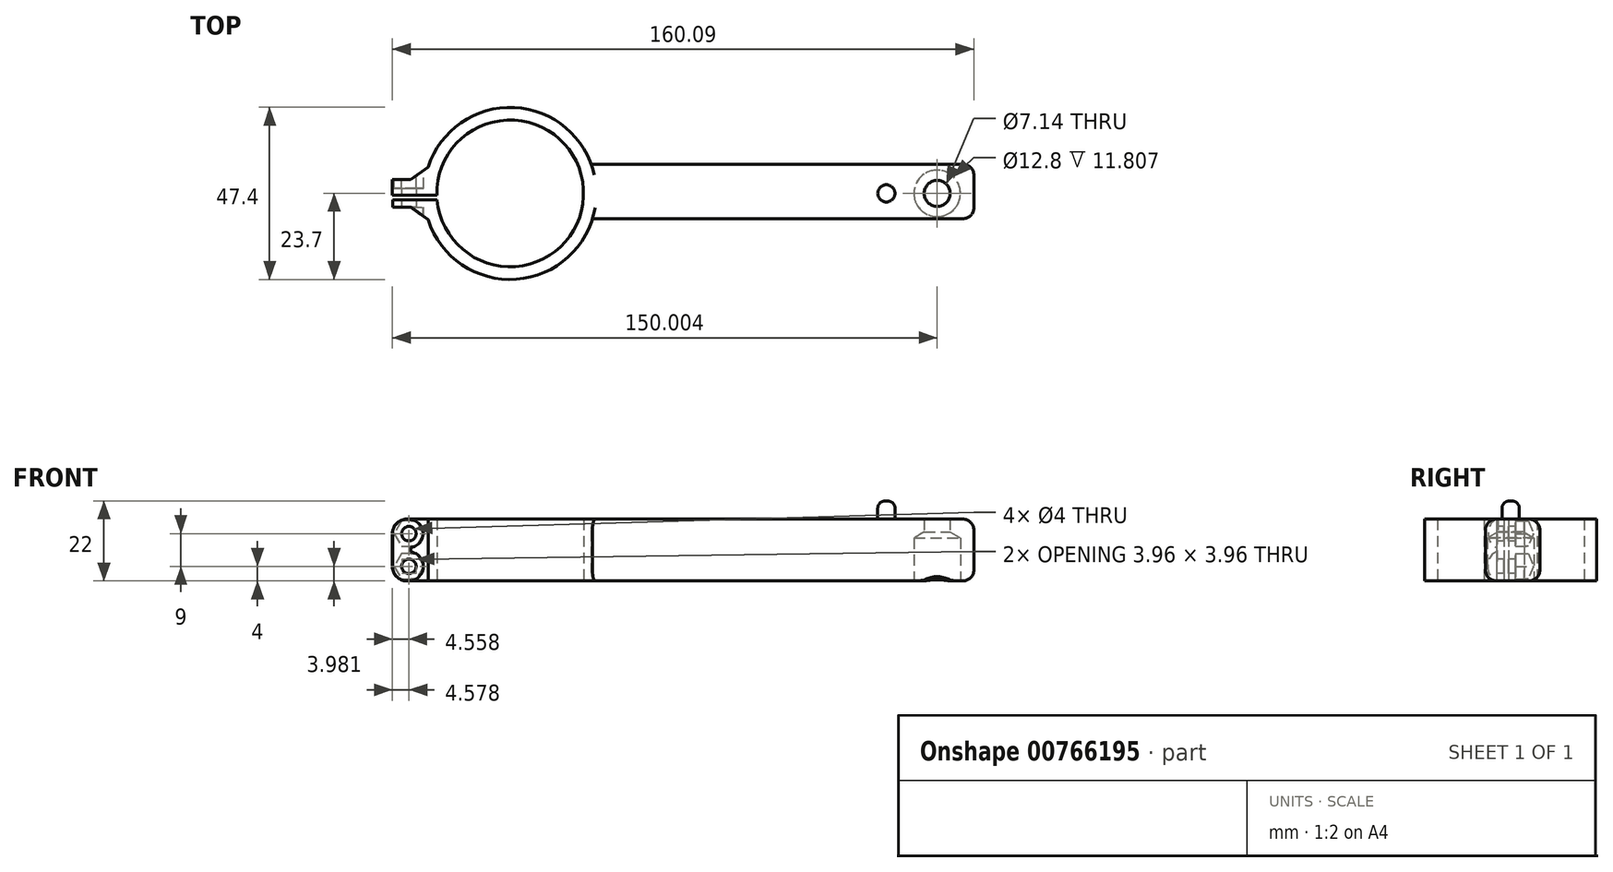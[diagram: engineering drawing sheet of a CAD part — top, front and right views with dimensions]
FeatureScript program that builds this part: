
annotation { "Feature Type Name" : "Feature", "Feature Type Description" : "" }
export const myFeature = defineFeature(function(context is Context, id is Id, definition is map)
    precondition{}
    {
        {
            var Q0;
            Q0=qCreatedBy(makeId("Top.planeOp"),FACE);
            var sketch = newSketch(context, id + "F0", { "sketchPlane" : qUnion([Q0])});
            skArc(sketch, "E0", {"start": v(-20.12, -1.8) * mm, "mid": v(20.17, 1.17) * mm, "end": v(-20.2, -0.54) * mm});
            skArc(sketch, "E1", {"start": v(-23.4, -3.8) * mm, "mid": v(-1.63, -23.64) * mm, "end": v(22.65, -6.97) * mm});
            skLineSegment(sketch, "E2", {"start": v(-23.7, -0.54) * mm, "end": v(-20.2, -0.54) * mm});
            skLineSegment(sketch, "E3", {"start": v(-23.63, -1.8) * mm, "end": v(-20.12, -1.8) * mm});
            skPoint(sketch, "E4.start.orphan", {"position": v(-23.7, 0) * mm});
            skLineSegment(sketch, "E5", {"start": v(-23.7, -0.54) * mm, "end": v(-32.44, -0.54) * mm});
            skLineSegment(sketch, "E6", {"start": v(-23.63, -1.8) * mm, "end": v(-32.38, -1.8) * mm});
            skLineSegment(sketch, "E7", {"start": v(-32.38, -1.8) * mm, "end": v(-32.38, -3.8) * mm});
            skLineSegment(sketch, "E8", {"start": v(-32.44, -0.54) * mm, "end": v(-32.44, 3.76) * mm});
            skLineSegment(sketch, "E9", {"start": v(-32.44, 3.76) * mm, "end": v(-23.4, 3.76) * mm});
            skLineSegment(sketch, "E10", {"start": v(-32.38, -3.8) * mm, "end": v(-23.4, -3.8) * mm});
            skPoint(sketch, "E11.startSnap0", {"position": v(23.7, 0.02) * mm});
            skLineSegment(sketch, "E12", {"start": v(127.65, 0.53) * mm, "end": v(127.65, 8.03) * mm});
            skLineSegment(sketch, "E13", {"start": v(127.65, 0.53) * mm, "end": v(127.65, -6.97) * mm});
            skLineSegment(sketch, "E14", {"start": v(127.65, 8.03) * mm, "end": v(22.3, 8.03) * mm});
            skLineSegment(sketch, "E15", {"start": v(127.65, -6.97) * mm, "end": v(22.65, -6.97) * mm});
            skArc(sketch, "E16.trimOffspring", {"start": v(22.3, 8.03) * mm, "mid": v(-2.2, 23.6) * mm, "end": v(-23.4, 3.76) * mm});
            skPoint(sketch, "E11.start.orphan", {"position": v(23.7, 0.02) * mm});
            skSolve(sketch);
        }
        {
            var Q0;
            Q0=makeQuery(id+"F0.imprint","IMPRINT",FACE,{"disambiguationData":[TD([[makeQuery(id+"F0.imprint","IMPRINT",EDGE,{"derivedFrom":sQuery(id+"F0.wireOp",EDGE,"E0")}),-1.0]])]});
            extrude(context, id + "F1", {"entities" : qUnion([Q0]), "depth" : 15 * mm, "offsetDistance" : 25 * mm});
        }
        {
            var Q0;
            Q0=makeQuery(id+"F1.opExtrude","CAP_FACE",FACE,{"disambiguationData":[OSD([sQuery(id+"F0.wireOp",EDGE,"E0"),sQuery(id+"F0.wireOp",EDGE,"E1"),sQuery(id+"F0.wireOp",EDGE,"E2"),sQuery(id+"F0.wireOp",EDGE,"E3"),sQuery(id+"F0.wireOp",EDGE,"E5"),sQuery(id+"F0.wireOp",EDGE,"E6"),sQuery(id+"F0.wireOp",EDGE,"E7"),sQuery(id+"F0.wireOp",EDGE,"E8"),sQuery(id+"F0.wireOp",EDGE,"E9"),sQuery(id+"F0.wireOp",EDGE,"E10"),sQuery(id+"F0.wireOp",EDGE,"E12"),sQuery(id+"F0.wireOp",EDGE,"E13"),sQuery(id+"F0.wireOp",EDGE,"E14"),sQuery(id+"F0.wireOp",EDGE,"E15"),sQuery(id+"F0.wireOp",EDGE,"E16.trimOffspring")])],"isStart":false});
            extrude(context, id + "F2", {"entities" : qUnion([Q0]), "operationType" : NewBodyOperationType.ADD, "depth" : 1 * mm, "offsetDistance" : 25 * mm});
        }
        {
            var Q0;
            Q0=makeQuery(id+"F1.opExtrude","CAP_FACE",FACE,{"disambiguationData":[OSD([sQuery(id+"F0.wireOp",EDGE,"E0"),sQuery(id+"F0.wireOp",EDGE,"E1"),sQuery(id+"F0.wireOp",EDGE,"E2"),sQuery(id+"F0.wireOp",EDGE,"E3"),sQuery(id+"F0.wireOp",EDGE,"E5"),sQuery(id+"F0.wireOp",EDGE,"E6"),sQuery(id+"F0.wireOp",EDGE,"E7"),sQuery(id+"F0.wireOp",EDGE,"E8"),sQuery(id+"F0.wireOp",EDGE,"E9"),sQuery(id+"F0.wireOp",EDGE,"E10"),sQuery(id+"F0.wireOp",EDGE,"E12"),sQuery(id+"F0.wireOp",EDGE,"E13"),sQuery(id+"F0.wireOp",EDGE,"E14"),sQuery(id+"F0.wireOp",EDGE,"E15"),sQuery(id+"F0.wireOp",EDGE,"E16.trimOffspring")])],"isStart":true});
            extrude(context, id + "F3", {"entities" : qUnion([Q0]), "operationType" : NewBodyOperationType.ADD, "depth" : 1 * mm, "offsetDistance" : 25 * mm});
        }
        {
            var Q0;
            {var subQ0=sQuery(id+"F0.wireOp",EDGE,"E10");Q0=makeQuery(id+"F3.boolean.opBoolean","MERGE",FACE,{"derivedFrom":[makeQuery(id+"F2.boolean.opBoolean","MERGE",FACE,{"derivedFrom":[makeQuery(id+"F1.opExtrude","SWEPT_FACE",FACE,{"disambiguationData":[OSD([subQ0])]}),makeQuery(id+"F2.opExtrude","SWEPT_FACE",FACE,{"disambiguationData":[OSD([subQ0])]})]}),makeQuery(id+"F3.opExtrude","SWEPT_FACE",FACE,{"disambiguationData":[OSD([subQ0])]})]});}
            var sketch = newSketch(context, id + "F4", { "sketchPlane" : qUnion([Q0])});
            skPoint(sketch, "E17", {"position": v(-27.88, 12) * mm});
            skPoint(sketch, "E18", {"position": v(-27.88, 3) * mm});
            skSolve(sketch);
        }
        {
            var Q0;
            Q0=sQuery(id+"F4.wireOp",VERTEX,"E17");
            var Q1;
            Q1=sQuery(id+"F4.wireOp",VERTEX,"E18");
            var Q2;
            Q2=makeQuery(id+"F1.opExtrude","SWEPT_BODY",BODY,{"disambiguationData":[OSD([sQuery(id+"F0.wireOp",EDGE,"E0"),sQuery(id+"F0.wireOp",EDGE,"E1"),sQuery(id+"F0.wireOp",EDGE,"E2"),sQuery(id+"F0.wireOp",EDGE,"E3"),sQuery(id+"F0.wireOp",EDGE,"E5"),sQuery(id+"F0.wireOp",EDGE,"E6"),sQuery(id+"F0.wireOp",EDGE,"E7"),sQuery(id+"F0.wireOp",EDGE,"E8"),sQuery(id+"F0.wireOp",EDGE,"E9"),sQuery(id+"F0.wireOp",EDGE,"E10")])]});
            hole(context, id + "F5", {"style" : HoleStyle.SIMPLE, "endStyle" : HoleEndStyle.THROUGH, "holeDiameter" : 4 * mm, "majorDiameter" : 5 * mm, "isTappedThrough" : true, "tappedDepth" : 12 * mm, "tapClearance" : 3, "locations" : qUnion([Q0, Q1]), "scope" : qUnion([Q2])});
        }
        {
            var Q0;
            Q0=makeQuery(id+"F2.opExtrude","CAP_EDGE",EDGE,{"disambiguationData":[OSD([sQuery(id+"F0.wireOp",EDGE,"E8")])],"isStart":false});
            var Q1;
            Q1=makeQuery(id+"F2.opExtrude","CAP_EDGE",EDGE,{"disambiguationData":[OSD([sQuery(id+"F0.wireOp",EDGE,"E7")])],"isStart":false});
            var Q2;
            Q2=makeQuery(id+"F3.opExtrude","CAP_EDGE",EDGE,{"disambiguationData":[OSD([sQuery(id+"F0.wireOp",EDGE,"E8")])],"isStart":false});
            var Q3;
            Q3=makeQuery(id+"F3.opExtrude","CAP_EDGE",EDGE,{"disambiguationData":[OSD([sQuery(id+"F0.wireOp",EDGE,"E7")])],"isStart":false});
            fillet(context, id + "F6", {"entities" : qUnion([Q0, Q1, Q2, Q3]), "radius" : 4 * mm, "tangentPropagation" : true, "allowEdgeOverflow" : false});
        }
        {
            var Q0;
            Q0=makeQuery(id+"F2.opExtrude","CAP_EDGE",EDGE,{"disambiguationData":[OSD([sQuery(id+"F0.wireOp",EDGE,"E15")])],"isStart":false});
            var Q1;
            Q1=makeQuery(id+"F2.opExtrude","CAP_EDGE",EDGE,{"disambiguationData":[OSD([sQuery(id+"F0.wireOp",EDGE,"E14")])],"isStart":false});
            var Q2;
            Q2=makeQuery(id+"F3.opExtrude","CAP_EDGE",EDGE,{"disambiguationData":[OSD([sQuery(id+"F0.wireOp",EDGE,"E15")])],"isStart":false});
            var Q3;
            Q3=makeQuery(id+"F3.opExtrude","CAP_EDGE",EDGE,{"disambiguationData":[OSD([sQuery(id+"F0.wireOp",EDGE,"E14")])],"isStart":false});
            var Q4;
            {var subQ0=sQuery(id+"F0.wireOp",EDGE,"E14");var subQ1=sQuery(id+"F0.wireOp",EDGE,"E12");Q4=makeQuery(id+"F3.boolean.opBoolean","MERGE",EDGE,{"derivedFrom":[makeQuery(id+"F2.boolean.opBoolean","MERGE",EDGE,{"derivedFrom":[makeQuery(id+"F1.opExtrude","SWEPT_EDGE",EDGE,{"disambiguationData":[OSD([subQ1,subQ0])]}),makeQuery(id+"F2.opExtrude","SWEPT_EDGE",EDGE,{"disambiguationData":[OSD([subQ1,subQ0])]})]}),makeQuery(id+"F3.opExtrude","SWEPT_EDGE",EDGE,{"disambiguationData":[OSD([subQ1,subQ0])]})]});}
            var Q5;
            Q5=makeQuery(id+"F3.opExtrude","CAP_EDGE",EDGE,{"disambiguationData":[OSD([sQuery(id+"F0.wireOp",EDGE,"E12"),sQuery(id+"F0.wireOp",EDGE,"E13")])],"isStart":false});
            var Q6;
            {var subQ0=sQuery(id+"F0.wireOp",EDGE,"E15");var subQ1=sQuery(id+"F0.wireOp",EDGE,"E13");Q6=makeQuery(id+"F3.boolean.opBoolean","MERGE",EDGE,{"derivedFrom":[makeQuery(id+"F2.boolean.opBoolean","MERGE",EDGE,{"derivedFrom":[makeQuery(id+"F1.opExtrude","SWEPT_EDGE",EDGE,{"disambiguationData":[OSD([subQ1,subQ0])]}),makeQuery(id+"F2.opExtrude","SWEPT_EDGE",EDGE,{"disambiguationData":[OSD([subQ1,subQ0])]})]}),makeQuery(id+"F3.opExtrude","SWEPT_EDGE",EDGE,{"disambiguationData":[OSD([subQ1,subQ0])]})]});}
            var Q7;
            Q7=makeQuery(id+"F2.opExtrude","CAP_EDGE",EDGE,{"disambiguationData":[OSD([sQuery(id+"F0.wireOp",EDGE,"E12"),sQuery(id+"F0.wireOp",EDGE,"E13")])],"isStart":false});
            fillet(context, id + "F7", {"entities" : qUnion([Q0, Q1, Q2, Q3, Q4, Q5, Q6, Q7]), "radius" : 3 * mm, "tangentPropagation" : true, "allowEdgeOverflow" : false});
        }
        {
            var Q0;
            Q0=makeQuery(id+"F1.opExtrude","SWEPT_FACE",FACE,{"disambiguationData":[OSD([sQuery(id+"F0.wireOp",EDGE,"E9")])]});
            var sketch = newSketch(context, id + "F8", { "sketchPlane" : qUnion([Q0])});
            skCircle(sketch, "E19.cCircle", {"center": v(27.88, 12) * mm, "radius": 3.5 * mm, "construction": true});
            skLineSegment(sketch, "E19.0", {"start": v(31.92, 11.98) * mm, "end": v(29.89, 8.5) * mm});
            skLineSegment(sketch, "E19.1", {"start": v(29.89, 8.5) * mm, "end": v(25.85, 8.5) * mm});
            skLineSegment(sketch, "E19.2", {"start": v(25.85, 8.5) * mm, "end": v(23.84, 12.02) * mm});
            skLineSegment(sketch, "E19.3", {"start": v(23.84, 12.02) * mm, "end": v(25.87, 15.5) * mm});
            skLineSegment(sketch, "E19.4", {"start": v(25.87, 15.5) * mm, "end": v(29.92, 15.5) * mm});
            skLineSegment(sketch, "E19.5", {"start": v(29.92, 15.5) * mm, "end": v(31.92, 11.98) * mm});
            skPoint(sketch, "E19.0.midPoint", {"position": v(30.9, 10.24) * mm});
            skCircle(sketch, "E20.cCircle", {"center": v(27.88, 3) * mm, "radius": 3.5 * mm, "construction": true});
            skLineSegment(sketch, "E20.0", {"start": v(31.92, 2.98) * mm, "end": v(29.88, -0.51) * mm});
            skLineSegment(sketch, "E20.1", {"start": v(29.88, -0.51) * mm, "end": v(25.84, -0.49) * mm});
            skLineSegment(sketch, "E20.2", {"start": v(25.84, -0.49) * mm, "end": v(23.84, 3.02) * mm});
            skLineSegment(sketch, "E20.3", {"start": v(23.84, 3.02) * mm, "end": v(25.88, 6.51) * mm});
            skLineSegment(sketch, "E20.4", {"start": v(25.88, 6.51) * mm, "end": v(29.92, 6.49) * mm});
            skLineSegment(sketch, "E20.5", {"start": v(29.92, 6.49) * mm, "end": v(31.92, 2.98) * mm});
            skPoint(sketch, "E20.0.midPoint", {"position": v(30.9, 1.23) * mm});
            skSolve(sketch);
        }
        {
            var Q0;
            {var subQ1=sQuery(id+"F8.wireOp",EDGE,"E19.0");Q0=makeQuery(id+"F8.imprint","IMPRINT",FACE,{"disambiguationData":[TD([[makeQuery(id+"F8.imprint","IMPRINT",EDGE,{"derivedFrom":subQ1}),-1.0]])]});}
            var Q1;
            {var subQ0=sQuery(id+"F8.wireOp",EDGE,"E20.2");Q1=makeQuery(id+"F8.imprint","IMPRINT",FACE,{"disambiguationData":[TD([[makeQuery(id+"F8.imprint","IMPRINT",EDGE,{"derivedFrom":subQ0}),-1.0]])]});}
            extrude(context, id + "F9", {"entities" : qUnion([Q0, Q1]), "operationType" : NewBodyOperationType.REMOVE, "oppositeDirection" : true, "depth" : 2.4 * mm, "offsetDistance" : 25 * mm});
        }
        {
            var Q0;
            Q0=makeQuery(id+"F3.opExtrude","CAP_FACE",FACE,{"disambiguationData":[OSD([sQuery(id+"F0.wireOp",EDGE,"E0"),sQuery(id+"F0.wireOp",EDGE,"E1"),sQuery(id+"F0.wireOp",EDGE,"E2"),sQuery(id+"F0.wireOp",EDGE,"E3"),sQuery(id+"F0.wireOp",EDGE,"E5"),sQuery(id+"F0.wireOp",EDGE,"E6"),sQuery(id+"F0.wireOp",EDGE,"E7"),sQuery(id+"F0.wireOp",EDGE,"E8"),sQuery(id+"F0.wireOp",EDGE,"E9"),sQuery(id+"F0.wireOp",EDGE,"E10"),sQuery(id+"F0.wireOp",EDGE,"E12"),sQuery(id+"F0.wireOp",EDGE,"E13"),sQuery(id+"F0.wireOp",EDGE,"E14"),sQuery(id+"F0.wireOp",EDGE,"E15"),sQuery(id+"F0.wireOp",EDGE,"E16.trimOffspring")])],"isStart":false});
            var sketch = newSketch(context, id + "F10", { "sketchPlane" : qUnion([Q0])});
            skPoint(sketch, "E21", {"position": v(117.56, 0) * mm});
            skSolve(sketch);
        }
        {
            var Q0;
            Q0=sQuery(id+"F10.wireOp",VERTEX,"E21");
            var Q1;
            Q1=makeQuery(id+"F1.opExtrude","SWEPT_BODY",BODY,{"disambiguationData":[OSD([sQuery(id+"F0.wireOp",EDGE,"E0"),sQuery(id+"F0.wireOp",EDGE,"E1"),sQuery(id+"F0.wireOp",EDGE,"E2"),sQuery(id+"F0.wireOp",EDGE,"E3"),sQuery(id+"F0.wireOp",EDGE,"E5"),sQuery(id+"F0.wireOp",EDGE,"E6"),sQuery(id+"F0.wireOp",EDGE,"E7"),sQuery(id+"F0.wireOp",EDGE,"E8"),sQuery(id+"F0.wireOp",EDGE,"E9"),sQuery(id+"F0.wireOp",EDGE,"E10"),sQuery(id+"F0.wireOp",EDGE,"E12"),sQuery(id+"F0.wireOp",EDGE,"E13"),sQuery(id+"F0.wireOp",EDGE,"E14"),sQuery(id+"F0.wireOp",EDGE,"E15"),sQuery(id+"F0.wireOp",EDGE,"E16.trimOffspring")])]});
            hole(context, id + "F11", {"style" : HoleStyle.SIMPLE, "endStyle" : HoleEndStyle.THROUGH, "standardTappedOrClearance" : lookupTablePath({ "fit" : "Normal (ASME)", "standard" : "ANSI", "size" : "1/4", "type" : "Clearance" }), "standardBlindInLast" : lookupTablePath({ "fit" : "Normal", "standard" : "ANSI", "size" : "1/4", "type" : "Clearance" }), "holeDiameter" : 7.14 * mm, "majorDiameter" : 5 * mm, "isTappedThrough" : true, "tappedDepth" : 12 * mm, "tapClearance" : 3, "locations" : qUnion([Q0]), "scope" : qUnion([Q1])});
        }
        {
            var Q0;
            Q0=sQuery(id+"F10.wireOp",VERTEX,"E21");
            var Q1;
            Q1=makeQuery(id+"F1.opExtrude","SWEPT_BODY",BODY,{"disambiguationData":[OSD([sQuery(id+"F0.wireOp",EDGE,"E0"),sQuery(id+"F0.wireOp",EDGE,"E1"),sQuery(id+"F0.wireOp",EDGE,"E2"),sQuery(id+"F0.wireOp",EDGE,"E3"),sQuery(id+"F0.wireOp",EDGE,"E5"),sQuery(id+"F0.wireOp",EDGE,"E6"),sQuery(id+"F0.wireOp",EDGE,"E7"),sQuery(id+"F0.wireOp",EDGE,"E8"),sQuery(id+"F0.wireOp",EDGE,"E9"),sQuery(id+"F0.wireOp",EDGE,"E10"),sQuery(id+"F0.wireOp",EDGE,"E12"),sQuery(id+"F0.wireOp",EDGE,"E13"),sQuery(id+"F0.wireOp",EDGE,"E14"),sQuery(id+"F0.wireOp",EDGE,"E15"),sQuery(id+"F0.wireOp",EDGE,"E16.trimOffspring")])]});
            hole(context, id + "F12", {"style" : HoleStyle.SIMPLE, "endStyle" : HoleEndStyle.BLIND, "holeDiameter" : 12.8 * mm, "majorDiameter" : 5 * mm, "holeDepth" : 10.57 * mm, "isTappedThrough" : true, "tappedDepth" : 12 * mm, "tapClearance" : 3, "locations" : qUnion([Q0]), "scope" : qUnion([Q1])});
        }
        {
            var Q0;
            Q0=makeQuery(id+"F2.opExtrude","CAP_FACE",FACE,{"disambiguationData":[OSD([sQuery(id+"F0.wireOp",EDGE,"E0"),sQuery(id+"F0.wireOp",EDGE,"E1"),sQuery(id+"F0.wireOp",EDGE,"E2"),sQuery(id+"F0.wireOp",EDGE,"E3"),sQuery(id+"F0.wireOp",EDGE,"E5"),sQuery(id+"F0.wireOp",EDGE,"E6"),sQuery(id+"F0.wireOp",EDGE,"E7"),sQuery(id+"F0.wireOp",EDGE,"E8"),sQuery(id+"F0.wireOp",EDGE,"E9"),sQuery(id+"F0.wireOp",EDGE,"E10"),sQuery(id+"F0.wireOp",EDGE,"E12"),sQuery(id+"F0.wireOp",EDGE,"E13"),sQuery(id+"F0.wireOp",EDGE,"E14"),sQuery(id+"F0.wireOp",EDGE,"E15"),sQuery(id+"F0.wireOp",EDGE,"E16.trimOffspring")])],"isStart":false});
            var sketch = newSketch(context, id + "F13", { "sketchPlane" : qUnion([Q0])});
            skCircle(sketch, "E22", {"center": v(103.58, 0) * mm, "radius": 2.38 * mm});
            skSolve(sketch);
        }
        {
            var Q0;
            Q0=makeQuery(id+"F13.imprint","IMPRINT",FACE,{"disambiguationData":[TD([[makeQuery(id+"F13.imprint","IMPRINT",EDGE,{"derivedFrom":sQuery(id+"F13.wireOp",EDGE,"E22")}),1.0]])]});
            extrude(context, id + "F14", {"entities" : qUnion([Q0]), "operationType" : NewBodyOperationType.ADD, "depth" : 5 * mm, "offsetDistance" : 25 * mm});
        }
        {
            var Q0;
            Q0=makeQuery(id+"F14.opExtrude","CAP_EDGE",EDGE,{"disambiguationData":[OSD([sQuery(id+"F13.wireOp",EDGE,"E22")])],"isStart":false});
            fillet(context, id + "F15", {"entities" : qUnion([Q0]), "radius" : 2 * mm, "tangentPropagation" : true, "allowEdgeOverflow" : false});
        }
        {
            var Q0;
            {var subQ0=sQuery(id+"F0.wireOp",EDGE,"E16.trimOffspring");var subQ1=sQuery(id+"F0.wireOp",EDGE,"E9");Q0=makeQuery(id+"F3.boolean.opBoolean","MERGE",EDGE,{"derivedFrom":[makeQuery(id+"F2.boolean.opBoolean","MERGE",EDGE,{"derivedFrom":[makeQuery(id+"F1.opExtrude","SWEPT_EDGE",EDGE,{"disambiguationData":[OSD([subQ1,subQ0])]}),makeQuery(id+"F2.opExtrude","SWEPT_EDGE",EDGE,{"disambiguationData":[OSD([subQ1,subQ0])]})]}),makeQuery(id+"F3.opExtrude","SWEPT_EDGE",EDGE,{"disambiguationData":[OSD([subQ1,subQ0])]})]});}
            var Q1;
            {var subQ0=sQuery(id+"F0.wireOp",EDGE,"E10");var subQ1=sQuery(id+"F0.wireOp",EDGE,"E1");Q1=makeQuery(id+"F3.boolean.opBoolean","MERGE",EDGE,{"derivedFrom":[makeQuery(id+"F2.boolean.opBoolean","MERGE",EDGE,{"derivedFrom":[makeQuery(id+"F1.opExtrude","SWEPT_EDGE",EDGE,{"disambiguationData":[OSD([subQ1,subQ0])]}),makeQuery(id+"F2.opExtrude","SWEPT_EDGE",EDGE,{"disambiguationData":[OSD([subQ1,subQ0])]})]}),makeQuery(id+"F3.opExtrude","SWEPT_EDGE",EDGE,{"disambiguationData":[OSD([subQ1,subQ0])]})]});}
            chamfer(context, id + "F16", {"entities" : qUnion([Q0, Q1]), "width" : 5 * mm, "tangentPropagation" : true});
        }
        {
            var Q0;
            {var subQ0=sQuery(id+"F0.wireOp",EDGE,"E10");Q0=makeQuery(id+"F4.imprint","IMPRINT",FACE,{"disambiguationData":[TD([[makeQuery(id+"F4.imprint","IMPRINT",EDGE,{"derivedFrom":makeQuery(id+"F2.opExtrude","CAP_EDGE",EDGE,{"disambiguationData":[OSD([subQ0])],"isStart":false})}),-1.0]])]});}
            var sketch = newSketch(context, id + "F17", { "sketchPlane" : qUnion([Q0])});
            skCircle(sketch, "E23", {"center": v(-27.88, 12.06) * mm, "radius": 3.92 * mm});
            skCircle(sketch, "E24", {"center": v(-27.85, 3.02) * mm, "radius": 4 * mm});
            skSolve(sketch);
        }
        {
            var Q0;
            Q0=makeQuery(id+"F17.imprint","IMPRINT",FACE,{"disambiguationData":[TD([[makeQuery(id+"F17.imprint","IMPRINT",EDGE,{"derivedFrom":sQuery(id+"F17.wireOp",EDGE,"E23")}),1.0]])]});
            var Q1;
            Q1=makeQuery(id+"F17.imprint","IMPRINT",FACE,{"disambiguationData":[TD([[makeQuery(id+"F17.imprint","IMPRINT",EDGE,{"derivedFrom":sQuery(id+"F17.wireOp",EDGE,"E24")}),1.0]])]});
            extrude(context, id + "F18", {"entities" : qUnion([Q0, Q1]), "operationType" : NewBodyOperationType.REMOVE, "depth" : 25 * mm, "offsetDistance" : 25 * mm});
        }
    });
